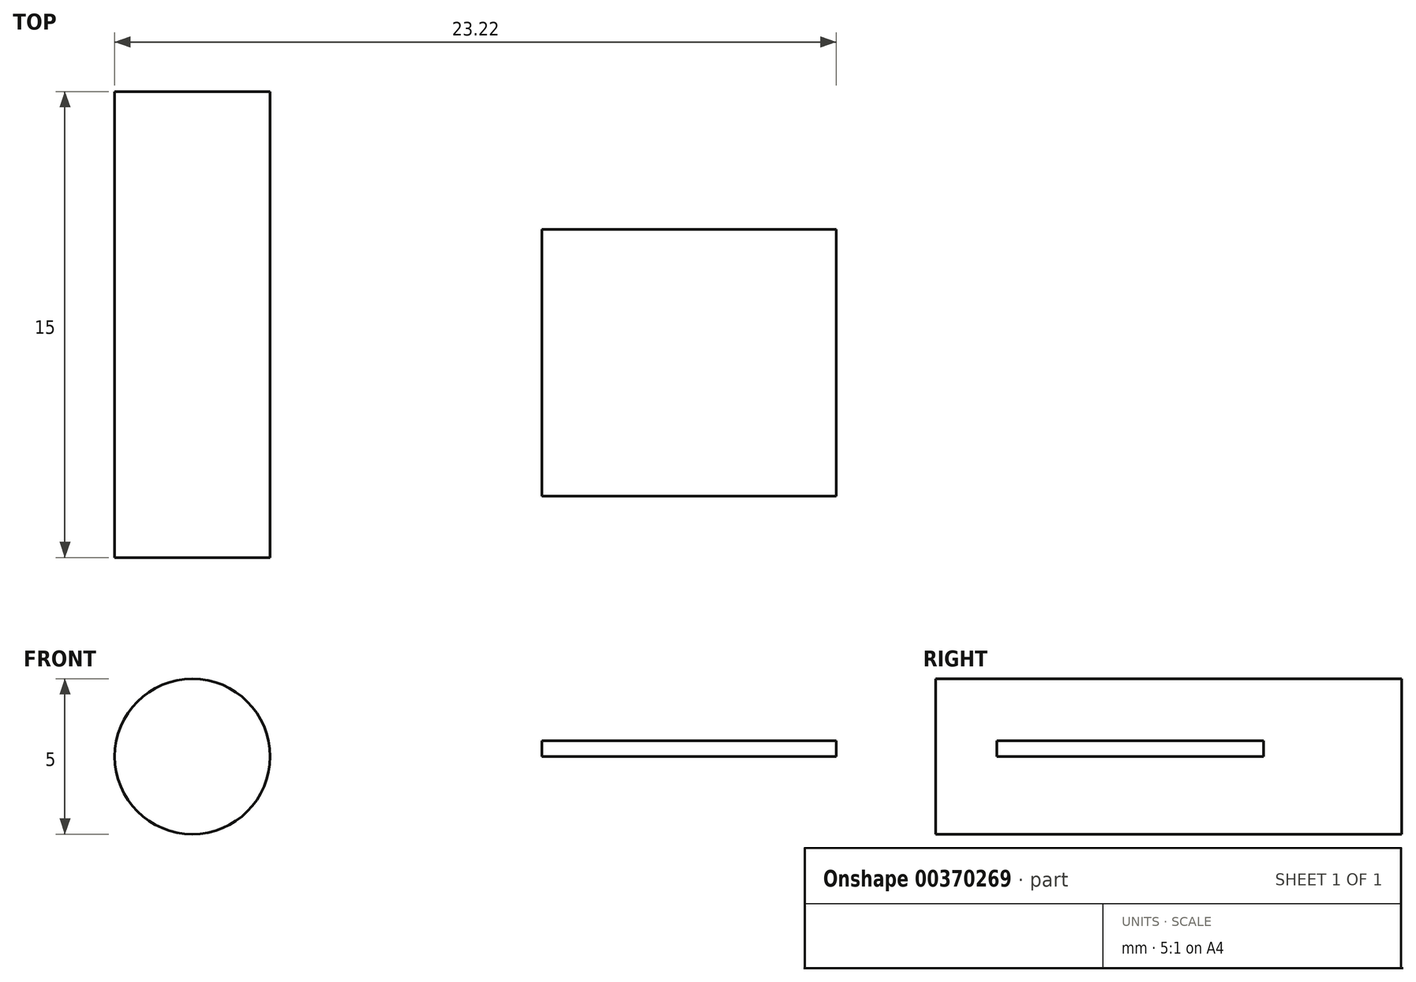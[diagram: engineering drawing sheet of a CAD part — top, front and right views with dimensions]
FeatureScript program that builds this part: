
annotation { "Feature Type Name" : "Feature", "Feature Type Description" : "" }
export const myFeature = defineFeature(function(context is Context, id is Id, definition is map)
    precondition{}
    {
        {
            var Q0;
            Q0=qCreatedBy(makeId("Front.planeOp"),FACE);
            var sketch = newSketch(context, id + "F0", { "sketchPlane" : qUnion([Q0])});
            skCircle(sketch, "E0", {"center": v(0, 0) * mm, "radius": 2.5 * mm});
            skSolve(sketch);
        }
        {
            var Q0;
            Q0=makeQuery(id+"F0.imprint","IMPRINT",FACE,{"disambiguationData":[TD([[makeQuery(id+"F0.imprint","IMPRINT",EDGE,{"derivedFrom":sQuery(id+"F0.wireOp",EDGE,"E0")}),1.0]])]});
            extrude(context, id + "F1", {"entities" : qUnion([Q0]), "depth" : 15 * mm});
        }
        {
            var Q0;
            Q0=qCreatedBy(makeId("Top.planeOp"),FACE);
            var sketch = newSketch(context, id + "F2", { "sketchPlane" : qUnion([Q0])});
            skLineSegment(sketch, "E1.bottom", {"start": v(11.25, -4.44) * mm, "end": v(20.72, -4.44) * mm});
            skLineSegment(sketch, "E1.top", {"start": v(11.25, -13.03) * mm, "end": v(20.72, -13.03) * mm});
            skLineSegment(sketch, "E1.left", {"start": v(11.25, -4.44) * mm, "end": v(11.25, -13.03) * mm});
            skLineSegment(sketch, "E1.right", {"start": v(20.72, -4.44) * mm, "end": v(20.72, -13.03) * mm});
            skSolve(sketch);
        }
        {
            var Q0;
            Q0 = qSketchRegion(id + "F2", true);
            extrude(context, id + "F3", {"entities" : qUnion([Q0]), "depth" : 0.5 * mm});
        }
    });
